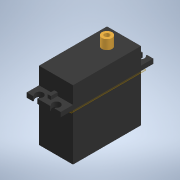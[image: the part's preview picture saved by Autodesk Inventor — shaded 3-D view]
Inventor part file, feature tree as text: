
AUTODESK INVENTOR PART (.ipt)
format: ipt  version: 2020 (Build 240168000, 168)  size: 201,728 bytes
history: native  units: in
note: dims shown in document units (in); Inventor stores cm internally (conversion verified against a paired STEP export)
features: extrude x6, sketch x6, projected_geometry x3, plane x1
ambient origin geometry x8: Origin, YZ Plane, XZ Plane, XY Plane, X Axis, Y Axis, Z Axis, Center Point
bodies: Solid1 (feature_tree)
feature tree (16):
  extrude  "Extrusion1"  Depth=1.5748in
  plane  "Work Plane1"
  extrude  "Extrusion2"  TaperAngle=0.0deg  [1 undecoded]
  extrude  "Extrusion3"  Depth=2.1457in
  extrude  "Extrusion4"  Depth=0.3937in
  extrude  "Extrusion5"  Depth=0.1063in TaperAngle=0.0deg
  extrude  "Extrusion6"  Depth=0.0787in
  sketch  "Sketch1"  dims[d0=0.7874in d1=1.5748in]
  sketch  "Sketch2"  dims[d2=1.0906in d3=0.0in d4=0.0in]
  projected_geometry  "Projected Loop1"
  sketch  "Sketch3"  dims[d5=0.5in d6=0.0in d7=2.1457in]
  projected_geometry  "Projected Loop2"
  sketch  "Sketch4"  dims[d8=0.3937in d9=1.9488in]
  sketch  "Sketch5"  dims[d10=0.1772in d11=0.1063in d12=0.0in]
  projected_geometry  "Projected Loop3"
  sketch  "Sketch6"  dims[d13=0.0984in d14=0.0787in d15=0.1575in d16=0.0787in d17=0.0in d18=0.2362in d19=1.1811in d20=0.2205in d21=0.0in d22=0.1181in d23=0.2205in d24=0.0in]
note: 1 required parameter value undecoded (feature->parameter linkage not recoverable at this tier; creation-order binding heuristic only, values carry confidence <= 0.55)
